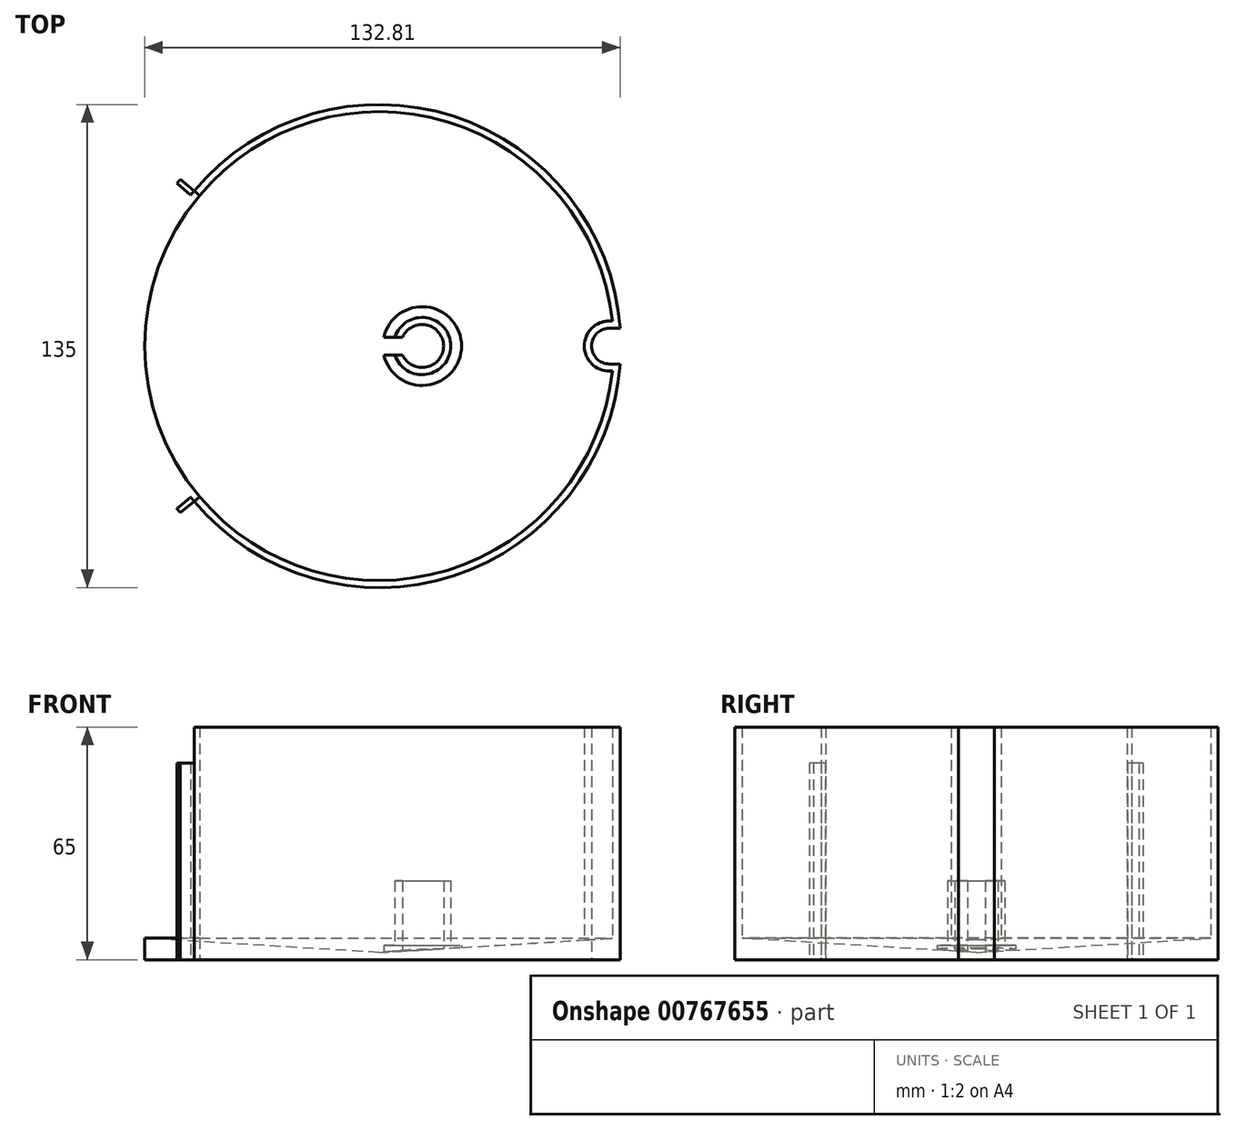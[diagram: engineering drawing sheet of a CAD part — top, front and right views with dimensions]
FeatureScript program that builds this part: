
annotation { "Feature Type Name" : "Feature", "Feature Type Description" : "" }
export const myFeature = defineFeature(function(context is Context, id is Id, definition is map)
    precondition{}
    {
        {
            var Q0;
            Q0=qCreatedBy(makeId("Top.planeOp"),FACE);
            var sketch = newSketch(context, id + "F0", { "sketchPlane" : qUnion([Q0])});
            skArc(sketch, "E0", {"start": v(65.12, 7) * mm, "mid": v(-65.5, 0) * mm, "end": v(65.12, -7) * mm});
            skArc(sketch, "E1", {"start": v(67.31, 5) * mm, "mid": v(20.72, 64.24) * mm, "end": v(-51.7, 43.39) * mm});
            skLineSegment(sketch, "E2", {"start": v(0, 0) * mm, "end": v(72.76, 0) * mm, "construction": true});
            skArc(sketch, "E3", {"start": v(64.31, 7) * mm, "mid": v(57.31, 0) * mm, "end": v(64.31, -7) * mm});
            skArc(sketch, "E4", {"start": v(64.31, 5) * mm, "mid": v(59.31, 0) * mm, "end": v(64.31, -5) * mm});
            skLineSegment(sketch, "E5", {"start": v(64.31, 7) * mm, "end": v(65.12, 7) * mm});
            skLineSegment(sketch, "E6", {"start": v(64.31, 5) * mm, "end": v(67.31, 5) * mm});
            skLineSegment(sketch, "E7", {"start": v(64.31, -5) * mm, "end": v(67.31, -5) * mm});
            skLineSegment(sketch, "E8", {"start": v(64.31, -7) * mm, "end": v(65.12, -7) * mm});
            skArc(sketch, "E9", {"start": v(-52.66, -42.23) * mm, "mid": v(-67.5, 0) * mm, "end": v(-52.66, 42.23) * mm});
            skLineSegment(sketch, "E10", {"start": v(-50.18, -42.1) * mm, "end": v(-55.54, -46.6) * mm});
            skLineSegment(sketch, "E11", {"start": v(-55.54, 46.6) * mm, "end": v(-50.18, 42.1) * mm});
            skLineSegment(sketch, "E12.0", {"start": v(-56.49, 45.44) * mm, "end": v(-52.66, 42.23) * mm});
            skArc(sketch, "E12.1", {"start": v(-56.49, -45.44) * mm, "mid": v(-72.5, 0) * mm, "end": v(-56.49, 45.44) * mm});
            skLineSegment(sketch, "E12.2", {"start": v(-52.66, -42.23) * mm, "end": v(-56.49, -45.44) * mm});
            skArc(sketch, "E13.trimOffspring", {"start": v(-51.7, -43.39) * mm, "mid": v(20.72, -64.24) * mm, "end": v(67.31, -5) * mm});
            skArc(sketch, "E14.trimOffspring", {"start": v(-52.66, 42.23) * mm, "mid": v(-67.5, 0) * mm, "end": v(-52.66, -42.23) * mm});
            skArc(sketch, "E15", {"start": v(-50.18, 42.1) * mm, "mid": v(-65.5, 0) * mm, "end": v(-50.18, -42.1) * mm});
            skArc(sketch, "E16", {"start": v(-56.49, -45.44) * mm, "mid": v(-56.02, -46.02) * mm, "end": v(-55.54, -46.6) * mm});
            skArc(sketch, "E17", {"start": v(-56.49, 45.44) * mm, "mid": v(-56.02, 46.02) * mm, "end": v(-55.54, 46.6) * mm});
            skPoint(sketch, "E18", {"position": v(-65.5, 0) * mm});
            skArc(sketch, "E19", {"start": v(-51.7, -43.39) * mm, "mid": v(-52.19, -42.81) * mm, "end": v(-52.66, -42.23) * mm});
            skArc(sketch, "E20", {"start": v(-52.66, 42.23) * mm, "mid": v(-52.19, 42.81) * mm, "end": v(-51.7, 43.39) * mm});
            skArc(sketch, "E21", {"start": v(67.31, -5) * mm, "mid": v(67.5, 0) * mm, "end": v(67.31, 5) * mm});
            skSolve(sketch);
        }
        {
            var Q0;
            Q0=qCreatedBy(makeId("Top.planeOp"),FACE);
            var sketch = newSketch(context, id + "F1", { "sketchPlane" : qUnion([Q0])});
            skArc(sketch, "E22", {"start": v(4.4, -2.5) * mm, "mid": v(20, 0) * mm, "end": v(4.4, 2.5) * mm});
            skArc(sketch, "E23", {"start": v(6.55, -2.5) * mm, "mid": v(18, 0) * mm, "end": v(6.55, 2.5) * mm});
            skArc(sketch, "E24", {"start": v(1.29, -2.5) * mm, "mid": v(23, 0) * mm, "end": v(1.29, 2.5) * mm});
            skLineSegment(sketch, "E25", {"start": v(6.55, 2.5) * mm, "end": v(1.29, 2.5) * mm});
            skLineSegment(sketch, "E26", {"start": v(6.55, -2.5) * mm, "end": v(1.29, -2.5) * mm});
            skArc(sketch, "E27", {"start": v(1.29, -2.5) * mm, "mid": v(1, 0) * mm, "end": v(1.29, 2.5) * mm, "construction": true});
            skLineSegment(sketch, "E28", {"start": v(12, 0) * mm, "end": v(0, 0) * mm, "construction": true});
            skSolve(sketch);
        }
        {
            var Q0;
            Q0=qCreatedBy(makeId("Front.planeOp"),FACE);
            var sketch = newSketch(context, id + "F2", { "sketchPlane" : qUnion([Q0])});
            skLineSegment(sketch, "E29", {"start": v(0, 0) * mm, "end": v(-65.5, 0) * mm});
            skLineSegment(sketch, "E30", {"start": v(-65.5, 0) * mm, "end": v(-65.5, 6) * mm});
            skLineSegment(sketch, "E31", {"start": v(-65.5, 6) * mm, "end": v(0, 2) * mm});
            skLineSegment(sketch, "E32", {"start": v(0, 2) * mm, "end": v(0, 0) * mm});
            skSolve(sketch);
        }
        {
            var Q0;
            Q0=makeQuery(id+"F2.imprint","IMPRINT",FACE,{"disambiguationData":[TD([[makeQuery(id+"F2.imprint","IMPRINT",EDGE,{"derivedFrom":sQuery(id+"F2.wireOp",EDGE,"E29")}),-1.0]])]});
            var Q1;
            Q1=sQuery(id+"F2.wireOp",EDGE,"E32");
            revolve(context, id + "F3", {"surfaceOperationType" : NewSurfaceOperationType.NEW, "entities" : qUnion([Q0]), "axis" : qUnion([Q1]), "revolveType" : RevolveType.FULL});
        }
        {
            var Q0;
            {var subQ9=sQuery(id+"F0.wireOp",EDGE,"E1");Q0=makeQuery(id+"F0.imprint","IMPRINT",FACE,{"disambiguationData":[TD([[makeQuery(id+"F0.imprint","IMPRINT",EDGE,{"derivedFrom":subQ9}),1.0]])]});}
            extrude(context, id + "F4", {"entities" : qUnion([Q0]), "operationType" : NewBodyOperationType.ADD, "depth" : 65 * mm, "offsetDistance" : 25 * mm});
        }
        {
            var Q0;
            Q0=makeQuery(id+"F0.imprint","IMPRINT",FACE,{"disambiguationData":[TD([[makeQuery(id+"F0.imprint","IMPRINT",EDGE,{"derivedFrom":sQuery(id+"F0.wireOp",EDGE,"E12.2")}),1.0]])]});
            var Q1;
            Q1=makeQuery(id+"F0.imprint","IMPRINT",FACE,{"disambiguationData":[TD([[makeQuery(id+"F0.imprint","IMPRINT",EDGE,{"derivedFrom":sQuery(id+"F0.wireOp",EDGE,"E14.trimOffspring")}),1.0]])]});
            var Q2;
            Q2=makeQuery(id+"F0.imprint","IMPRINT",FACE,{"disambiguationData":[TD([[makeQuery(id+"F0.imprint","IMPRINT",EDGE,{"derivedFrom":sQuery(id+"F0.wireOp",EDGE,"E12.0")}),1.0]])]});
            extrude(context, id + "F5", {"entities" : qUnion([Q0, Q1, Q2]), "operationType" : NewBodyOperationType.ADD, "depth" : 55 * mm, "offsetDistance" : 25 * mm});
        }
        {
            var Q0;
            Q0=makeQuery(id+"F0.imprint","IMPRINT",FACE,{"disambiguationData":[TD([[makeQuery(id+"F0.imprint","IMPRINT",EDGE,{"derivedFrom":sQuery(id+"F0.wireOp",EDGE,"E4")}),1.0]])]});
            extrude(context, id + "F6", {"entities" : qUnion([Q0]), "operationType" : NewBodyOperationType.REMOVE, "endBound" : BoundingType.THROUGH_ALL, "depth" : 25 * mm, "offsetDistance" : 25 * mm});
        }
        {
            var Q0;
            {var subQ0=sQuery(id+"F1.wireOp",EDGE,"E22");Q0=makeQuery(id+"F1.imprint","IMPRINT",FACE,{"disambiguationData":[TD([[makeQuery(id+"F1.imprint","IMPRINT",EDGE,{"derivedFrom":subQ0}),1.0]])]});}
            extrude(context, id + "F7", {"entities" : qUnion([Q0]), "operationType" : NewBodyOperationType.ADD, "depth" : 22 * mm, "offsetDistance" : 25 * mm});
        }
        {
            var Q0;
            {var subQ0=sQuery(id+"F1.wireOp",EDGE,"E22");Q0=makeQuery(id+"F1.imprint","IMPRINT",FACE,{"disambiguationData":[TD([[makeQuery(id+"F1.imprint","IMPRINT",EDGE,{"derivedFrom":subQ0}),-1.0]])]});}
            extrude(context, id + "F8", {"entities" : qUnion([Q0]), "operationType" : NewBodyOperationType.ADD, "depth" : 4 * mm, "offsetDistance" : 25 * mm});
        }
    });
